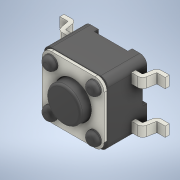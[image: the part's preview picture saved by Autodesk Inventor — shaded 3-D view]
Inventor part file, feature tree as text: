
AUTODESK INVENTOR PART (.ipt)
format: ipt  version: 2020 (Build 240168000, 168)  size: 573,952 bytes
history: native  units: mm
features: extrude x1, sketch x1, imported_body x1
ambient origin geometry x8: Origin, YZ Plane, XZ Plane, XY Plane, X Axis, Y Axis, Z Axis, Center Point
bodies: Solid1 (feature_tree)
feature tree (3):
  extrude  "Extrusion1"  Depth=0.5mm
  sketch  "Sketch1"  dims[d1=0.5mm d2=0.5mm d3=0.5mm d4=0.5mm d7=0.05mm d8=0.2mm d9=0.0mm]
  imported_body  "Base1"
